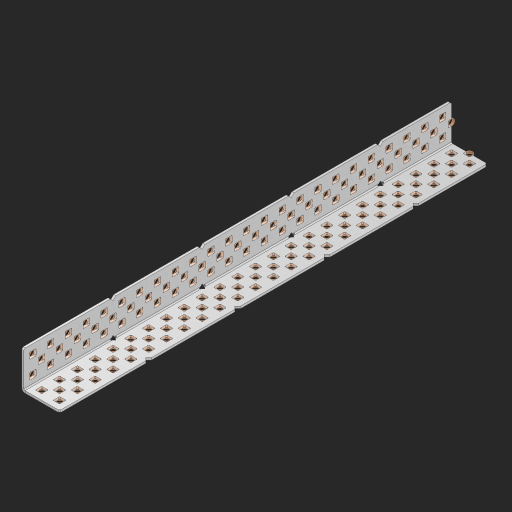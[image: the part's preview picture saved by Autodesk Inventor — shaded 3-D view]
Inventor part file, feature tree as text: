
AUTODESK INVENTOR PART (.ipt)
format: ipt  version: 2023 (Build 270158000, 158)  size: 1,750,528 bytes
history: native  units: in
note: dims shown in document units (in); Inventor stores cm internally (conversion verified against a paired STEP export)
features: other x150, extrude x142, sheet_metal_op x8, sketch x7, pattern_linear x2, mirror x1, chamfer x1
ambient origin geometry x8: Origin, YZ Plane, XZ Plane, XY Plane, X Axis, Y Axis, Z Axis, Center Point
bodies: Solid1 (feature_tree), Body (feature_tree)
feature tree (311):
  sheet_metal_op  "Flanges"
  sheet_metal_op  "Body Pattern"
  pattern_linear  "Center Pattern"  Spacing1=1.0in  [1 undecoded]
  other  "Arc Length"
  pattern_linear  "Notch Pattern"  Spacing1=0.25in  [1 undecoded]
  other  "Diagonal Plane"
  mirror  "Everything Mirrored"
  chamfer  "End Chamfer"
  sketch  "Sketch1"  dims[d0=1.0in]
  other  "Plate1"
  sketch  "Sketch2"  dims[d1=12.0in]
  other  "Plate2"
  sheet_metal_op  "Bend1"
  sheet_metal_op  "Corner1"
  sketch  "Sketch8"  dims[d2=0.0625in]
  sketch  "Sketch9"  dims[d3=0.0625in]
  other  "Srf91"
  sheet_metal_op  "Body Pattern Sketch"
  other  "Srf92"
  sketch  "Sketch13"  dims[d4=0.0312in]
  sketch  "Sketch15"  dims[d5=0.125in]
  sketch  "Sketch16"  dims[d6=0.0625in d7=1.0in d8=90.0deg d9=0.0312in d10=0.25in d11=0.0625in d12=0.0625in d49=0.182in d50=0.02in d52=0.25in d53=0.0625in d54=0.0in d55=0.172in d56=1.0in d57=0.0in d60=9.4488in d62=0.5in d63=0.7874in d65=0.5in d85=0.1473in d86=0.1782in d89=0.0625in d90=0.0in d91=0.04in d92=0.0491in d95=2.5in d96=0.04in d97=0.25in d98=45.0deg d99=0.25in d106=0.182in d107=0.02in d108=0.5in d110=0.0625in d111=0.0in d112=0.172in d113=0.5in d114=0.0in d117=0.5in d123=0.25in d125=0.25in d126=0.0491in d127=0.1473in d128=0.08in d129=0.04in d130=2.5in]
  other  "Srf786"
  other  "Srf856"
  other  "Srf857"
  other  "Srf858"
  other  "Srf859"
  other  "Srf860"
  other  "Srf861"
  other  "Srf889"
  other  "Srf890"
  other  "Srf891"
  other  "Srf1275"
  other  "Srf1276"
  other  "Srf1278"
  other  "Srf1279"
  other  "Srf1280"
  other  "Srf1281"
  other  "Srf1282"
  other  "Srf1283"
  other  "Srf1277"
  other  "Srf1285"
  other  "Srf1286"
  other  "Srf1287"
  other  "Srf1383"
  other  "Srf1384"
  other  "Srf1385"
  other  "Srf1386"
  other  "Srf1387"
  other  "Srf1388"
  other  "Srf1389"
  other  "Srf1390"
  other  "Srf1391"
  other  "Srf1392"
  other  "Srf1393"
  other  "Srf1394"
  other  "Srf1395"
  other  "Srf1396"
  other  "Srf1397"
  other  "Srf1398"
  other  "Srf1399"
  other  "Srf1400"
  other  "Srf1401"
  other  "Srf1402"
  other  "Srf1403"
  other  "Srf1404"
  other  "Srf1405"
  other  "Srf1406"
  other  "Srf1407"
  other  "Srf1408"
  other  "Srf1409"
  other  "Srf1410"
  other  "Srf1411"
  other  "Srf1412"
  other  "Srf1413"
  other  "Srf1414"
  other  "Srf1415"
  other  "Srf1416"
  other  "Srf1417"
  other  "Srf1418"
  other  "Srf1419"
  other  "Srf1420"
  other  "Srf1421"
  other  "Srf1422"
  other  "Srf1445"
  other  "Srf1446"
  other  "Srf1447"
  other  "Srf1448"
  other  "Srf1449"
  other  "Srf1450"
  other  "Srf1451"
  other  "Srf1452"
  other  "Srf1453"
  other  "Srf1454"
  other  "Srf1455"
  other  "Srf1456"
  other  "Srf1457"
  other  "Srf1458"
  other  "Srf1459"
  other  "Srf1460"
  other  "Srf1461"
  other  "Srf1462"
  other  "Srf1463"
  other  "Srf1464"
  other  "Srf1475"
  other  "Srf1476"
  other  "Srf1477"
  other  "Srf1478"
  other  "Srf1479"
  other  "Srf1480"
  other  "Srf1481"
  other  "Srf1482"
  other  "Srf1483"
  other  "Srf1484"
  other  "Srf1485"
  other  "Srf1486"
  other  "Srf1487"
  other  "Srf1488"
  other  "Srf1489"
  other  "Srf1490"
  other  "Srf1491"
  other  "Srf1492"
  other  "Srf1493"
  other  "Srf1494"
  other  "Srf1495"
  other  "Srf1496"
  other  "Srf1497"
  other  "Srf1498"
  other  "Srf1499"
  other  "Srf1500"
  other  "Srf1501"
  other  "Srf1502"
  other  "Srf1503"
  other  "Srf1504"
  other  "Srf1505"
  other  "Srf1506"
  other  "Srf1507"
  other  "Srf1508"
  other  "Srf1509"
  other  "Srf1510"
  other  "Srf1511"
  other  "Srf1512"
  other  "Srf1513"
  other  "Srf1514"
  other  "Srf1537"
  other  "Srf1538"
  other  "Srf1539"
  other  "Srf1540"
  other  "Srf1541"
  other  "Srf1542"
  other  "Srf1543"
  other  "Srf1544"
  other  "Srf1545"
  other  "Srf1546"
  other  "Srf1547"
  other  "Srf1548"
  other  "Srf1549"
  other  "Srf1550"
  other  "Srf1551"
  other  "Srf1552"
  other  "Srf1553"
  other  "Srf1554"
  other  "Srf1555"
  other  "Srf1556"
  sheet_metal_op  "Body Stamp"
  sheet_metal_op  "Body Circle"
  other  "Center Stamp"
  other  "Center Circle"
  sheet_metal_op  "Notch"
  extrude  "ExtrusionSrf92"  Depth=0.0625in
  extrude  "ExtrusionSrf856"  Depth=0.0625in
  extrude  "ExtrusionSrf857"  Depth=0.182in
  extrude  "ExtrusionSrf858"  Depth=0.02in
  extrude  "ExtrusionSrf859"  Depth=0.25in
  extrude  "ExtrusionSrf860"  Depth=0.0625in
  extrude  "ExtrusionSrf861"  TaperAngle=0.0deg  [1 undecoded]
  extrude  "ExtrusionSrf889"  Depth=2.5in
  extrude  "ExtrusionSrf890"  Depth=1.0in TaperAngle=0.0deg
  extrude  "ExtrusionSrf891"  Depth=2.5in
  extrude  "ExtrusionSrf1275"  Depth=0.5in
  extrude  "ExtrusionSrf1276"  Depth=2.5in
  extrude  "ExtrusionSrf1277"  Depth=2.5in
  extrude  "ExtrusionSrf1278"  Depth=0.0625in
  extrude  "ExtrusionSrf1279"  Depth=2.5in TaperAngle=0.0deg
  extrude  "ExtrusionSrf1280"  Depth=2.5in
  extrude  "ExtrusionSrf1281"  Depth=0.25in TaperAngle=45.0deg
  extrude  "ExtrusionSrf1282"  Depth=0.25in
  extrude  "ExtrusionSrf1345"  Depth=0.182in
  extrude  "ExtrusionSrf1346"  Depth=0.02in
  extrude  "ExtrusionSrf1347"  Depth=0.5in
  extrude  "ExtrusionSrf1348"  Depth=0.0625in
  extrude  "ExtrusionSrf1383"  TaperAngle=0.0deg  [1 undecoded]
  extrude  "ExtrusionSrf1384"  Depth=2.5in
  extrude  "ExtrusionSrf1385"  Depth=0.5in TaperAngle=0.0deg
  extrude  "ExtrusionSrf1386"  Depth=0.5in
  extrude  "ExtrusionSrf1387"  Depth=0.25in
  extrude  "ExtrusionSrf1388"  Depth=0.25in
  extrude  "ExtrusionSrf1389"  Depth=2.5in
  extrude  "ExtrusionSrf1390"  Depth=2.5in
  extrude  "ExtrusionSrf1391"  Depth=2.5in
  extrude  "ExtrusionSrf1392"  Depth=2.5in
  extrude  "ExtrusionSrf1393"  Depth=2.5in
  extrude  "ExtrusionSrf1394"  [1 undecoded]
  extrude  "ExtrusionSrf1395"  [1 undecoded]
  extrude  "ExtrusionSrf1396"  [1 undecoded]
  extrude  "ExtrusionSrf1397"  [1 undecoded]
  extrude  "ExtrusionSrf1398"  [1 undecoded]
  extrude  "ExtrusionSrf1399"  [1 undecoded]
  extrude  "ExtrusionSrf1400"  [1 undecoded]
  extrude  "ExtrusionSrf1401"  [1 undecoded]
  extrude  "ExtrusionSrf1402"  [1 undecoded]
  extrude  "ExtrusionSrf1403"  [1 undecoded]
  extrude  "ExtrusionSrf1404"  [1 undecoded]
  extrude  "ExtrusionSrf1405"  [1 undecoded]
  extrude  "ExtrusionSrf1406"  [1 undecoded]
  extrude  "ExtrusionSrf1407"  [1 undecoded]
  extrude  "ExtrusionSrf1408"  [1 undecoded]
  extrude  "ExtrusionSrf1409"  [1 undecoded]
  extrude  "ExtrusionSrf1410"  [1 undecoded]
  extrude  "ExtrusionSrf1411"  [1 undecoded]
  extrude  "ExtrusionSrf1412"  [1 undecoded]
  extrude  "ExtrusionSrf1413"  [1 undecoded]
  extrude  "ExtrusionSrf1414"  [1 undecoded]
  extrude  "ExtrusionSrf1415"  [1 undecoded]
  extrude  "ExtrusionSrf1416"  [1 undecoded]
  extrude  "ExtrusionSrf1417"  [1 undecoded]
  extrude  "ExtrusionSrf1418"  [1 undecoded]
  extrude  "ExtrusionSrf1419"  [1 undecoded]
  extrude  "ExtrusionSrf1420"  [1 undecoded]
  extrude  "ExtrusionSrf1421"  [1 undecoded]
  extrude  "ExtrusionSrf1422"  [1 undecoded]
  extrude  "ExtrusionSrf1445"  [1 undecoded]
  extrude  "ExtrusionSrf1446"  [1 undecoded]
  extrude  "ExtrusionSrf1447"  [1 undecoded]
  extrude  "ExtrusionSrf1448"  [1 undecoded]
  extrude  "ExtrusionSrf1449"  [1 undecoded]
  extrude  "ExtrusionSrf1450"  [1 undecoded]
  extrude  "ExtrusionSrf1451"  [1 undecoded]
  extrude  "ExtrusionSrf1452"  [1 undecoded]
  extrude  "ExtrusionSrf1453"  [1 undecoded]
  extrude  "ExtrusionSrf1454"  [1 undecoded]
  extrude  "ExtrusionSrf1455"  [1 undecoded]
  extrude  "ExtrusionSrf1456"  [1 undecoded]
  extrude  "ExtrusionSrf1457"  [1 undecoded]
  extrude  "ExtrusionSrf1458"  [1 undecoded]
  extrude  "ExtrusionSrf1459"  [1 undecoded]
  extrude  "ExtrusionSrf1460"  [1 undecoded]
  extrude  "ExtrusionSrf1461"  [1 undecoded]
  extrude  "ExtrusionSrf1462"  [1 undecoded]
  extrude  "ExtrusionSrf1463"  [1 undecoded]
  extrude  "ExtrusionSrf1464"  [1 undecoded]
  extrude  "ExtrusionSrf1475"  [1 undecoded]
  extrude  "ExtrusionSrf1476"  [1 undecoded]
  extrude  "ExtrusionSrf1477"  [1 undecoded]
  extrude  "ExtrusionSrf1478"  [1 undecoded]
  extrude  "ExtrusionSrf1479"  [1 undecoded]
  extrude  "ExtrusionSrf1480"  [1 undecoded]
  extrude  "ExtrusionSrf1481"  [1 undecoded]
  extrude  "ExtrusionSrf1482"  [1 undecoded]
  extrude  "ExtrusionSrf1483"  [1 undecoded]
  extrude  "ExtrusionSrf1484"  [1 undecoded]
  extrude  "ExtrusionSrf1485"  [1 undecoded]
  extrude  "ExtrusionSrf1486"  [1 undecoded]
  extrude  "ExtrusionSrf1487"  [1 undecoded]
  extrude  "ExtrusionSrf1488"  [1 undecoded]
  extrude  "ExtrusionSrf1489"  [1 undecoded]
  extrude  "ExtrusionSrf1490"  [1 undecoded]
  extrude  "ExtrusionSrf1491"  [1 undecoded]
  extrude  "ExtrusionSrf1492"  [1 undecoded]
  extrude  "ExtrusionSrf1493"  [1 undecoded]
  extrude  "ExtrusionSrf1494"  [1 undecoded]
  extrude  "ExtrusionSrf1495"  [1 undecoded]
  extrude  "ExtrusionSrf1496"  [1 undecoded]
  extrude  "ExtrusionSrf1497"  [1 undecoded]
  extrude  "ExtrusionSrf1498"  [1 undecoded]
  extrude  "ExtrusionSrf1499"  [1 undecoded]
  extrude  "ExtrusionSrf1500"  [1 undecoded]
  extrude  "ExtrusionSrf1501"  [1 undecoded]
  extrude  "ExtrusionSrf1502"  [1 undecoded]
  extrude  "ExtrusionSrf1503"  [1 undecoded]
  extrude  "ExtrusionSrf1504"  [1 undecoded]
  extrude  "ExtrusionSrf1505"  [1 undecoded]
  extrude  "ExtrusionSrf1506"  [1 undecoded]
  extrude  "ExtrusionSrf1507"  [1 undecoded]
  extrude  "ExtrusionSrf1508"  [1 undecoded]
  extrude  "ExtrusionSrf1509"  [1 undecoded]
  extrude  "ExtrusionSrf1510"  [1 undecoded]
  extrude  "ExtrusionSrf1511"  [1 undecoded]
  extrude  "ExtrusionSrf1512"  [1 undecoded]
  extrude  "ExtrusionSrf1513"  [1 undecoded]
  extrude  "ExtrusionSrf1514"  [1 undecoded]
  extrude  "ExtrusionSrf1537"  [1 undecoded]
  extrude  "ExtrusionSrf1538"  [1 undecoded]
  extrude  "ExtrusionSrf1539"  [1 undecoded]
  extrude  "ExtrusionSrf1540"  [1 undecoded]
  extrude  "ExtrusionSrf1541"  [1 undecoded]
  extrude  "ExtrusionSrf1542"  [1 undecoded]
  extrude  "ExtrusionSrf1543"  [1 undecoded]
  extrude  "ExtrusionSrf1544"  [1 undecoded]
  extrude  "ExtrusionSrf1545"  [1 undecoded]
  extrude  "ExtrusionSrf1546"  [1 undecoded]
  extrude  "ExtrusionSrf1547"  [1 undecoded]
  extrude  "ExtrusionSrf1548"  [1 undecoded]
  extrude  "ExtrusionSrf1549"  [1 undecoded]
  extrude  "ExtrusionSrf1550"  [1 undecoded]
  extrude  "ExtrusionSrf1551"  [1 undecoded]
  extrude  "ExtrusionSrf1552"  [1 undecoded]
  extrude  "ExtrusionSrf1553"  [1 undecoded]
  extrude  "ExtrusionSrf1554"  [1 undecoded]
  extrude  "ExtrusionSrf1555"  [1 undecoded]
  extrude  "ExtrusionSrf1556"  [1 undecoded]
note: 113 required parameter values undecoded (feature->parameter linkage not recoverable at this tier; creation-order binding heuristic only, values carry confidence <= 0.55)
